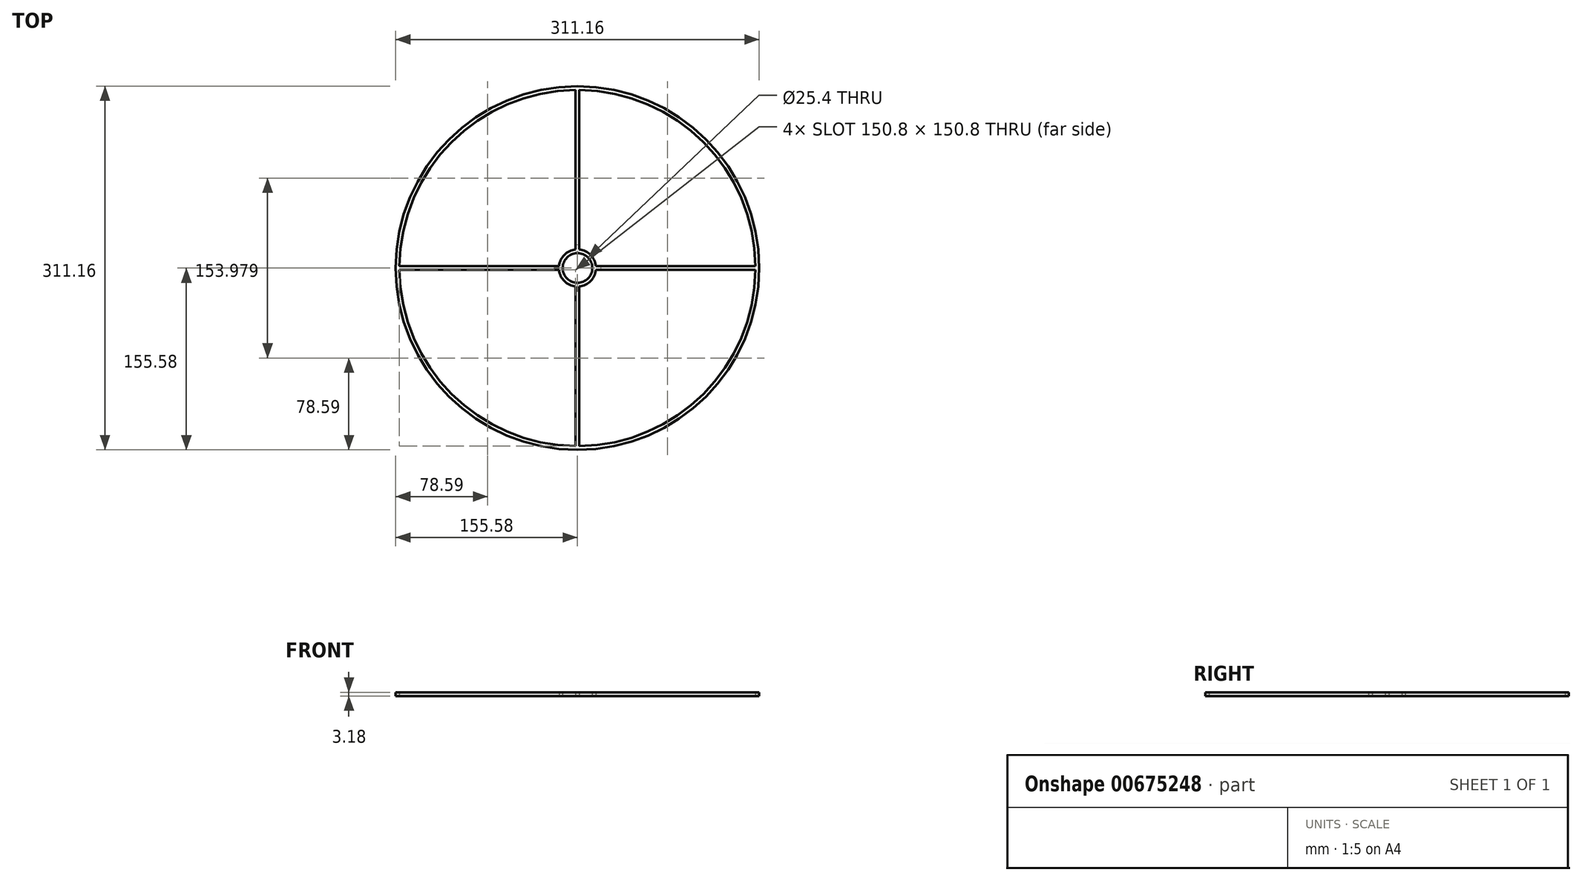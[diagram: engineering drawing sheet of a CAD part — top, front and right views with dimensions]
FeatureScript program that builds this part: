
annotation { "Feature Type Name" : "Feature", "Feature Type Description" : "" }
export const myFeature = defineFeature(function(context is Context, id is Id, definition is map)
    precondition{}
    {
        {
            var Q0;
            Q0=qCreatedBy(makeId("Top.planeOp"),FACE);
            var sketch = newSketch(context, id + "F0", { "sketchPlane" : qUnion([Q0])});
            skArc(sketch, "E0", {"start": v(-1.59, 152.4) * mm, "mid": v(-107.76, 107.76) * mm, "end": v(-152.4, 1.59) * mm});
            skCircle(sketch, "E1.0", {"center": v(0, 0) * mm, "radius": 155.58 * mm});
            skCircle(sketch, "E2", {"center": v(0, 0) * mm, "radius": 12.7 * mm});
            skArc(sketch, "E3.0", {"start": v(-1.59, 15.8) * mm, "mid": v(-11.23, 11.23) * mm, "end": v(-15.8, 1.59) * mm});
            skLineSegment(sketch, "E4.bottom", {"start": v(1.59, 1.59) * mm, "end": v(-1.59, 1.59) * mm});
            skLineSegment(sketch, "E4.top", {"start": v(1.59, -1.59) * mm, "end": v(-1.59, -1.59) * mm});
            skLineSegment(sketch, "E4.left", {"start": v(1.59, 1.59) * mm, "end": v(1.59, -1.59) * mm});
            skLineSegment(sketch, "E4.right", {"start": v(-1.59, 1.59) * mm, "end": v(-1.59, -1.59) * mm});
            skLineSegment(sketch, "E5", {"start": v(-1.59, 1.59) * mm, "end": v(-1.59, 152.4) * mm, "construction": true});
            skLineSegment(sketch, "E6", {"start": v(-1.59, 1.59) * mm, "end": v(-152.4, 1.59) * mm, "construction": true});
            skLineSegment(sketch, "E7", {"start": v(1.59, 1.59) * mm, "end": v(1.59, 152.4) * mm, "construction": true});
            skLineSegment(sketch, "E8", {"start": v(1.59, 1.59) * mm, "end": v(152.4, 1.59) * mm, "construction": true});
            skLineSegment(sketch, "E9", {"start": v(1.59, -1.59) * mm, "end": v(152.4, -1.59) * mm, "construction": true});
            skLineSegment(sketch, "E10", {"start": v(-1.59, -1.59) * mm, "end": v(-1.59, -152.4) * mm, "construction": true});
            skLineSegment(sketch, "E11", {"start": v(1.59, -1.59) * mm, "end": v(1.59, -152.4) * mm, "construction": true});
            skLineSegment(sketch, "E12", {"start": v(-1.59, -152.4) * mm, "end": v(-1.59, -15.8) * mm});
            skLineSegment(sketch, "E13", {"start": v(1.59, -152.4) * mm, "end": v(1.59, -15.8) * mm});
            skLineSegment(sketch, "E14", {"start": v(-1.59, -1.59) * mm, "end": v(-152.4, -1.59) * mm, "construction": true});
            skLineSegment(sketch, "E15", {"start": v(-152.4, -1.59) * mm, "end": v(-15.8, -1.59) * mm});
            skLineSegment(sketch, "E16", {"start": v(-152.4, 1.59) * mm, "end": v(-15.8, 1.59) * mm});
            skLineSegment(sketch, "E17", {"start": v(-1.59, 152.4) * mm, "end": v(-1.59, 15.8) * mm});
            skLineSegment(sketch, "E18", {"start": v(1.59, 152.4) * mm, "end": v(1.59, 15.8) * mm});
            skLineSegment(sketch, "E19", {"start": v(152.4, 1.59) * mm, "end": v(15.8, 1.59) * mm});
            skLineSegment(sketch, "E20", {"start": v(152.4, -1.59) * mm, "end": v(15.8, -1.59) * mm});
            skArc(sketch, "E21.trimOffspring", {"start": v(15.8, 1.59) * mm, "mid": v(11.23, 11.23) * mm, "end": v(1.59, 15.8) * mm});
            skArc(sketch, "E22.trimOffspring", {"start": v(-15.8, -1.59) * mm, "mid": v(-11.23, -11.23) * mm, "end": v(-1.59, -15.8) * mm});
            skArc(sketch, "E23.trimOffspring", {"start": v(152.4, 1.59) * mm, "mid": v(107.76, 107.76) * mm, "end": v(1.59, 152.4) * mm});
            skArc(sketch, "E24.trimOffspring", {"start": v(1.59, -15.8) * mm, "mid": v(11.23, -11.23) * mm, "end": v(15.8, -1.59) * mm});
            skArc(sketch, "E25.trimOffspring", {"start": v(1.59, -152.4) * mm, "mid": v(107.76, -107.76) * mm, "end": v(152.4, -1.59) * mm});
            skArc(sketch, "E26.trimOffspring", {"start": v(-152.4, -1.59) * mm, "mid": v(-107.76, -107.76) * mm, "end": v(-1.59, -152.4) * mm});
            skSolve(sketch);
        }
        {
            var Q0;
            Q0=makeQuery(id+"F0.imprint","IMPRINT",FACE,{"disambiguationData":[TD([[makeQuery(id+"F0.imprint","IMPRINT",EDGE,{"derivedFrom":sQuery(id+"F0.wireOp",EDGE,"E0")}),-1.0]])]});
            extrude(context, id + "F1", {"entities" : qUnion([Q0]), "depth" : 3.17 * mm, "offsetDistance" : 25.4 * mm});
        }
    });
